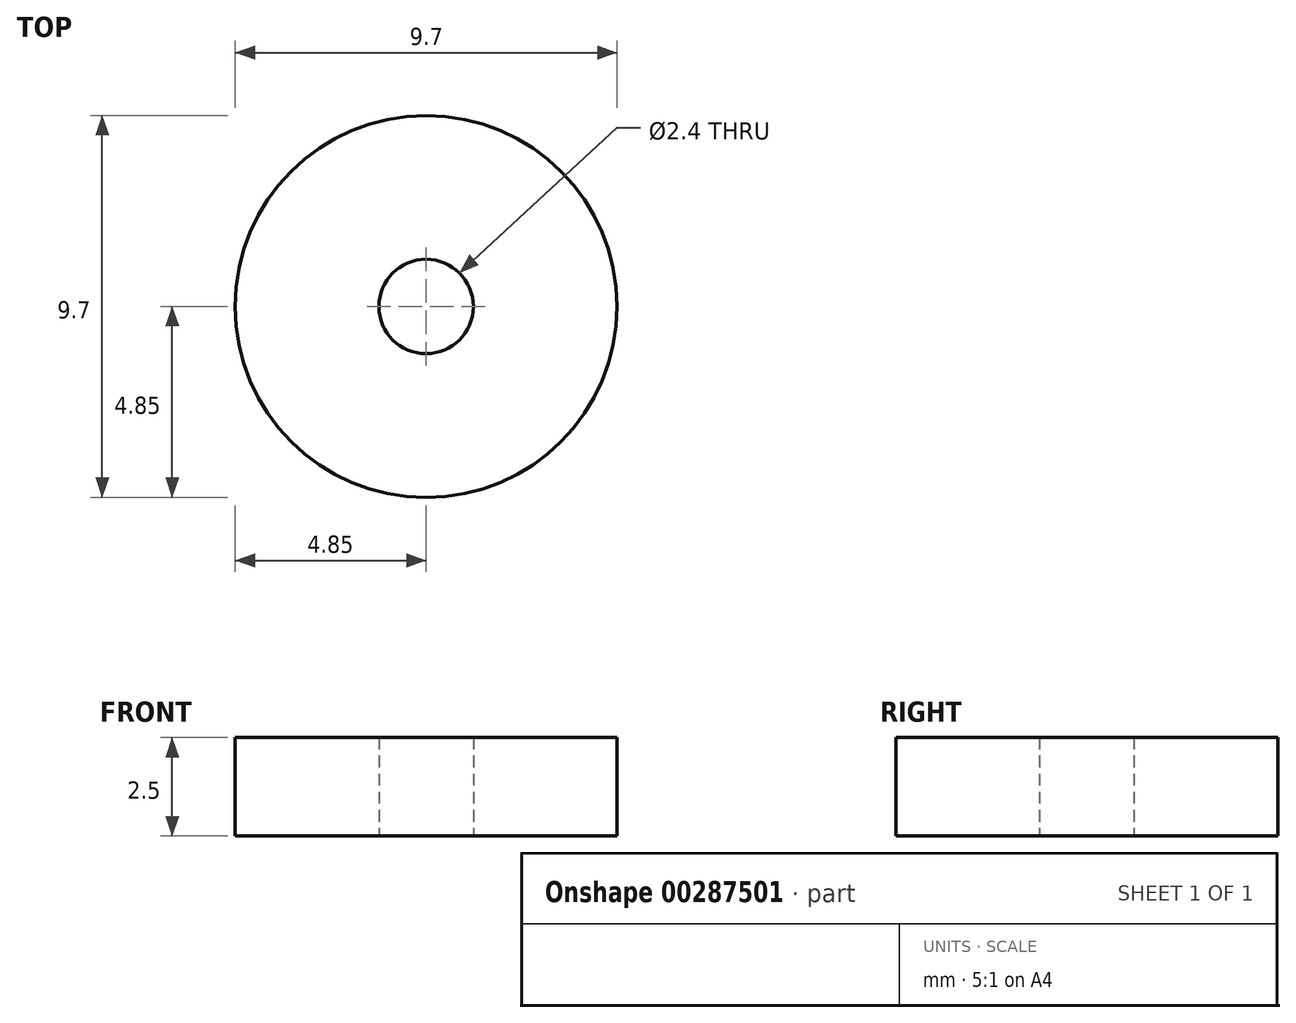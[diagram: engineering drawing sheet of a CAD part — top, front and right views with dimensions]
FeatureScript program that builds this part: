
annotation { "Feature Type Name" : "Feature", "Feature Type Description" : "" }
export const myFeature = defineFeature(function(context is Context, id is Id, definition is map)
    precondition{}
    {
        {
            var Q0;
            Q0=qCreatedBy(makeId("Top.planeOp"),FACE);
            var sketch = newSketch(context, id + "F0", { "sketchPlane" : qUnion([Q0])});
            skCircle(sketch, "E0", {"center": v(0, 0) * mm, "radius": 4.85 * mm});
            skSolve(sketch);
        }
        {
            var Q0;
            Q0=makeQuery(id+"F0.imprint","IMPRINT",FACE,{"disambiguationData":[TD([[makeQuery(id+"F0.imprint","IMPRINT",EDGE,{"derivedFrom":sQuery(id+"F0.wireOp",EDGE,"E0")}),1.0]])]});
            extrude(context, id + "F1", {"entities" : qUnion([Q0]), "depth" : 2.5 * mm});
        }
        {
            var Q0;
            Q0=makeQuery(id+"F1.opExtrude","CAP_FACE",FACE,{"disambiguationData":[OSD([sQuery(id+"F0.wireOp",EDGE,"E0")])],"isStart":true});
            var sketch = newSketch(context, id + "F2", { "sketchPlane" : qUnion([Q0])});
            skCircle(sketch, "E1", {"center": v(0, 0) * mm, "radius": 1.2 * mm});
            skSolve(sketch);
        }
        {
            var Q0;
            Q0 = qSketchRegion(id + "F2", true);
            extrude(context, id + "F3", {"entities" : qUnion([Q0]), "operationType" : NewBodyOperationType.REMOVE, "oppositeDirection" : true, "depth" : 25 * mm});
        }
    });
